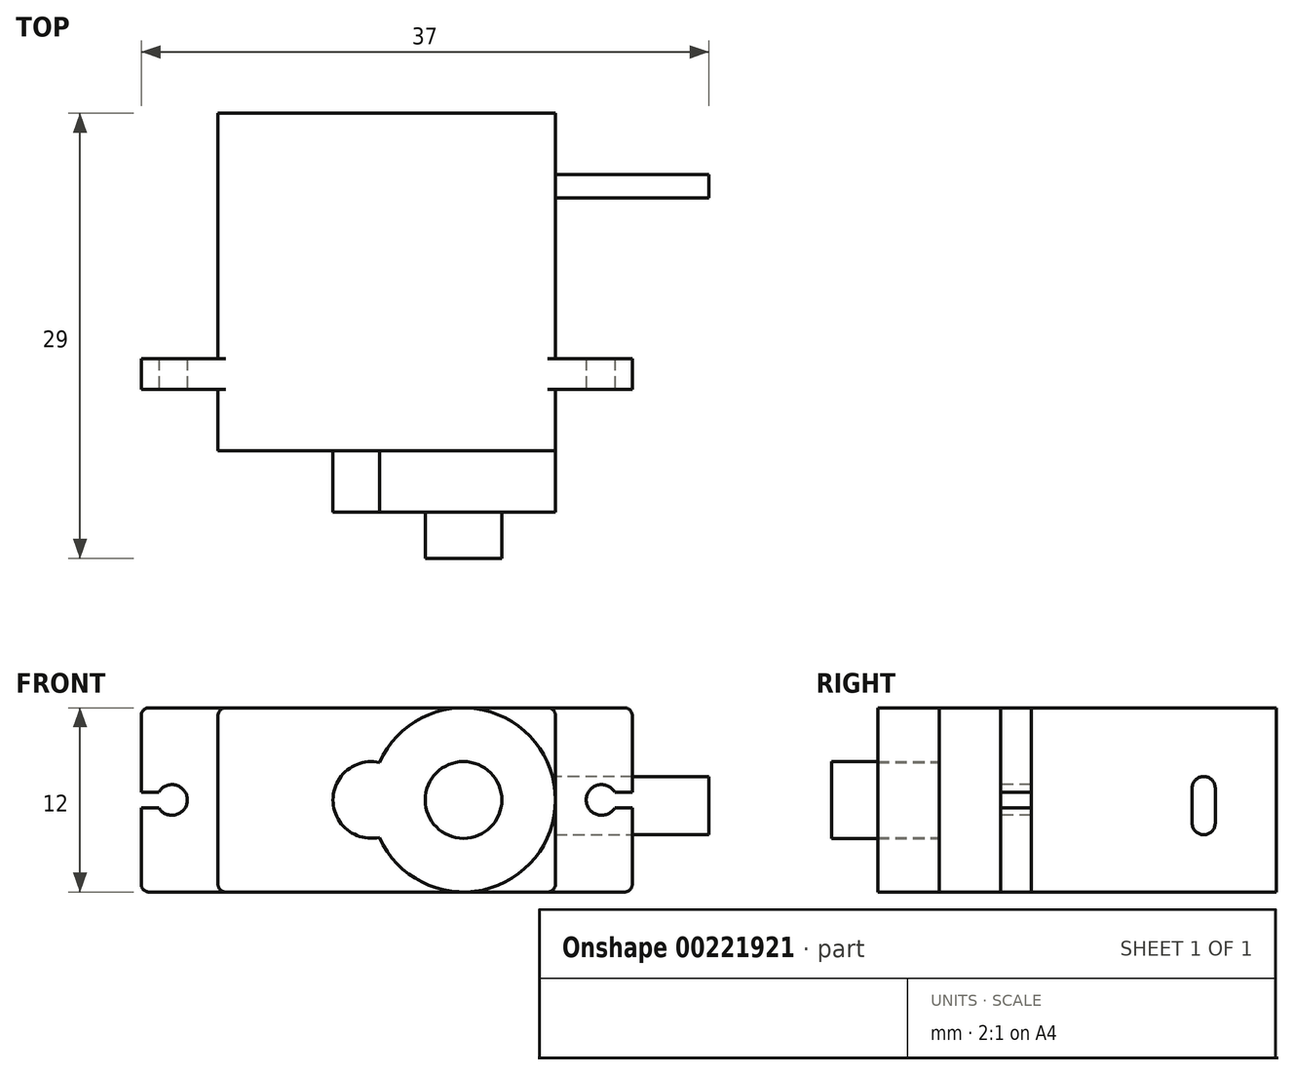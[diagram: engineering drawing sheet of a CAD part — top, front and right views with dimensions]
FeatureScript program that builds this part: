
annotation { "Feature Type Name" : "Feature", "Feature Type Description" : "" }
export const myFeature = defineFeature(function(context is Context, id is Id, definition is map)
    precondition{}
    {
        {
            var Q0;
            Q0=qCreatedBy(makeId("Top.planeOp"),FACE);
            var sketch = newSketch(context, id + "F0", { "sketchPlane" : qUnion([Q0])});
            skLineSegment(sketch, "E0.bottom", {"start": v(11, -11) * mm, "end": v(-11, -11) * mm});
            skLineSegment(sketch, "E0.top", {"start": v(11, 11) * mm, "end": v(-11, 11) * mm});
            skLineSegment(sketch, "E0.left", {"start": v(11, -11) * mm, "end": v(11, 11) * mm});
            skLineSegment(sketch, "E0.right", {"start": v(-11, -11) * mm, "end": v(-11, 11) * mm});
            skPoint(sketch, "E0.middle", {"position": v(0, 0) * mm});
            skLineSegment(sketch, "E1.bottom", {"start": v(-11, -7) * mm, "end": v(-16, -7) * mm});
            skLineSegment(sketch, "E1.top", {"start": v(-11, -5) * mm, "end": v(-16, -5) * mm});
            skLineSegment(sketch, "E1.left", {"start": v(-11, -7) * mm, "end": v(-11, -5) * mm});
            skLineSegment(sketch, "E1.right", {"start": v(-16, -7) * mm, "end": v(-16, -5) * mm});
            skLineSegment(sketch, "E2.bottom", {"start": v(11, -5) * mm, "end": v(16, -5) * mm});
            skLineSegment(sketch, "E2.top", {"start": v(11, -7) * mm, "end": v(16, -7) * mm});
            skLineSegment(sketch, "E2.left", {"start": v(11, -5) * mm, "end": v(11, -7) * mm});
            skLineSegment(sketch, "E2.right", {"start": v(16, -5) * mm, "end": v(16, -7) * mm});
            skSolve(sketch);
        }
        {
            var Q0;
            Q0 = qSketchRegion(id + "F0", true);
            extrude(context, id + "F1", {"entities" : qUnion([Q0]), "depth" : 12 * mm});
        }
        {
            var Q0;
            {var subQ0=sQuery(id+"F0.wireOp",EDGE,"E0.left");Q0=makeQuery(id+"F1.opExtrude","CAP_EDGE",EDGE,{"disambiguationData":[OSD([subQ0]),TDD([makeQuery(id+"F0.imprint","IMPRINT",EDGE,{"disambiguationData":[TD([[makeQuery(id+"F0.imprint","INTERSECT",VERTEX,{"derivedFrom":[sQuery(id+"F0.wireOp",EDGE,"E0.top"),subQ0]}),1.0]])],"derivedFrom":subQ0})])],"isStart":false});}
            var Q1;
            {var subQ0=sQuery(id+"F0.wireOp",EDGE,"E0.left");Q1=makeQuery(id+"F1.opExtrude","CAP_EDGE",EDGE,{"disambiguationData":[OSD([subQ0]),TDD([makeQuery(id+"F0.imprint","IMPRINT",EDGE,{"disambiguationData":[TD([[makeQuery(id+"F0.imprint","INTERSECT",VERTEX,{"derivedFrom":[sQuery(id+"F0.wireOp",EDGE,"E0.bottom"),subQ0]}),-1.0]])],"derivedFrom":subQ0})])],"isStart":false});}
            var Q2;
            {var subQ0=sQuery(id+"F0.wireOp",EDGE,"E0.right");Q2=makeQuery(id+"F1.opExtrude","CAP_EDGE",EDGE,{"disambiguationData":[OSD([subQ0]),TDD([makeQuery(id+"F0.imprint","IMPRINT",EDGE,{"disambiguationData":[TD([[makeQuery(id+"F0.imprint","INTERSECT",VERTEX,{"derivedFrom":[sQuery(id+"F0.wireOp",EDGE,"E0.bottom"),subQ0]}),-1.0]])],"derivedFrom":subQ0})])],"isStart":false});}
            var Q3;
            Q3=makeQuery(id+"F1.opExtrude","CAP_EDGE",EDGE,{"disambiguationData":[OSD([sQuery(id+"F0.wireOp",EDGE,"E2.right")])],"isStart":false});
            var Q4;
            {var subQ0=sQuery(id+"F0.wireOp",EDGE,"E0.right");Q4=makeQuery(id+"F1.opExtrude","CAP_EDGE",EDGE,{"disambiguationData":[OSD([subQ0]),TDD([makeQuery(id+"F0.imprint","IMPRINT",EDGE,{"disambiguationData":[TD([[makeQuery(id+"F0.imprint","INTERSECT",VERTEX,{"derivedFrom":[sQuery(id+"F0.wireOp",EDGE,"E0.top"),subQ0]}),1.0]])],"derivedFrom":subQ0})])],"isStart":false});}
            var Q5;
            Q5=makeQuery(id+"F1.opExtrude","CAP_EDGE",EDGE,{"disambiguationData":[OSD([sQuery(id+"F0.wireOp",EDGE,"E1.right")])],"isStart":false});
            var Q6;
            {var subQ0=sQuery(id+"F0.wireOp",EDGE,"E0.right");Q6=makeQuery(id+"F1.opExtrude","CAP_EDGE",EDGE,{"disambiguationData":[OSD([subQ0]),TDD([makeQuery(id+"F0.imprint","IMPRINT",EDGE,{"disambiguationData":[TD([[makeQuery(id+"F0.imprint","INTERSECT",VERTEX,{"derivedFrom":[sQuery(id+"F0.wireOp",EDGE,"E0.top"),subQ0]}),1.0]])],"derivedFrom":subQ0})])],"isStart":true});}
            var Q7;
            {var subQ0=sQuery(id+"F0.wireOp",EDGE,"E0.right");Q7=makeQuery(id+"F1.opExtrude","CAP_EDGE",EDGE,{"disambiguationData":[OSD([subQ0]),TDD([makeQuery(id+"F0.imprint","IMPRINT",EDGE,{"disambiguationData":[TD([[makeQuery(id+"F0.imprint","INTERSECT",VERTEX,{"derivedFrom":[sQuery(id+"F0.wireOp",EDGE,"E0.bottom"),subQ0]}),-1.0]])],"derivedFrom":subQ0})])],"isStart":true});}
            var Q8;
            Q8=makeQuery(id+"F1.opExtrude","CAP_EDGE",EDGE,{"disambiguationData":[OSD([sQuery(id+"F0.wireOp",EDGE,"E1.right")])],"isStart":true});
            var Q9;
            {var subQ0=sQuery(id+"F0.wireOp",EDGE,"E0.left");Q9=makeQuery(id+"F1.opExtrude","CAP_EDGE",EDGE,{"disambiguationData":[OSD([subQ0]),TDD([makeQuery(id+"F0.imprint","IMPRINT",EDGE,{"disambiguationData":[TD([[makeQuery(id+"F0.imprint","INTERSECT",VERTEX,{"derivedFrom":[sQuery(id+"F0.wireOp",EDGE,"E0.bottom"),subQ0]}),-1.0]])],"derivedFrom":subQ0})])],"isStart":true});}
            var Q10;
            {var subQ0=sQuery(id+"F0.wireOp",EDGE,"E0.left");Q10=makeQuery(id+"F1.opExtrude","CAP_EDGE",EDGE,{"disambiguationData":[OSD([subQ0]),TDD([makeQuery(id+"F0.imprint","IMPRINT",EDGE,{"disambiguationData":[TD([[makeQuery(id+"F0.imprint","INTERSECT",VERTEX,{"derivedFrom":[sQuery(id+"F0.wireOp",EDGE,"E0.top"),subQ0]}),1.0]])],"derivedFrom":subQ0})])],"isStart":true});}
            var Q11;
            Q11=makeQuery(id+"F1.opExtrude","CAP_EDGE",EDGE,{"disambiguationData":[OSD([sQuery(id+"F0.wireOp",EDGE,"E2.right")])],"isStart":true});
            fillet(context, id + "F2", {"entities" : qUnion([Q0, Q1, Q2, Q3, Q4, Q5, Q6, Q7, Q8, Q9, Q10, Q11]), "radius" : 0.5 * mm, "tangentPropagation" : true, "allowEdgeOverflow" : false});
        }
        {
            var Q0;
            Q0=makeQuery(id+"F1.opExtrude","SWEPT_FACE",FACE,{"disambiguationData":[OSD([sQuery(id+"F0.wireOp",EDGE,"E0.bottom")])]});
            var sketch = newSketch(context, id + "F3", { "sketchPlane" : qUnion([Q0])});
            skCircle(sketch, "E3", {"center": v(5, 6) * mm, "radius": 6 * mm});
            skCircle(sketch, "E4", {"center": v(-1, 6) * mm, "radius": 2.5 * mm});
            skSolve(sketch);
        }
        {
            var Q0;
            Q0 = qSketchRegion(id + "F3", true);
            extrude(context, id + "F4", {"entities" : qUnion([Q0]), "operationType" : NewBodyOperationType.ADD, "depth" : 4 * mm});
        }
        {
            var Q0;
            Q0=makeQuery(id+"F4.opExtrude","CAP_FACE",FACE,{"disambiguationData":[OSD([sQuery(id+"F3.wireOp",EDGE,"E3"),sQuery(id+"F3.wireOp",EDGE,"E4")])],"isStart":false});
            var sketch = newSketch(context, id + "F5", { "sketchPlane" : qUnion([Q0])});
            skCircle(sketch, "E5", {"center": v(5, 6) * mm, "radius": 2.5 * mm});
            skSolve(sketch);
        }
        {
            var Q0;
            Q0=makeQuery(id+"F5.imprint","IMPRINT",FACE,{"disambiguationData":[TD([[makeQuery(id+"F5.imprint","IMPRINT",EDGE,{"derivedFrom":sQuery(id+"F5.wireOp",EDGE,"E5")}),1.0]])]});
            extrude(context, id + "F6", {"entities" : qUnion([Q0]), "depth" : 3 * mm});
        }
        {
            var Q0;
            {var subQ0=sQuery(id+"F0.wireOp",EDGE,"E0.left");Q0=makeQuery(id+"F1.opExtrude","SWEPT_FACE",FACE,{"disambiguationData":[OSD([subQ0]),TDD([makeQuery(id+"F0.imprint","IMPRINT",EDGE,{"disambiguationData":[TD([[makeQuery(id+"F0.imprint","INTERSECT",VERTEX,{"derivedFrom":[sQuery(id+"F0.wireOp",EDGE,"E0.top"),subQ0]}),1.0]])],"derivedFrom":subQ0})])]});}
            var sketch = newSketch(context, id + "F7", { "sketchPlane" : qUnion([Q0])});
            skLineSegment(sketch, "E6.bottom", {"start": v(5.5, 3.73) * mm, "end": v(7, 3.73) * mm});
            skLineSegment(sketch, "E6.top", {"start": v(5.5, 7.53) * mm, "end": v(7, 7.53) * mm});
            skLineSegment(sketch, "E6.left", {"start": v(5.5, 3.73) * mm, "end": v(5.5, 7.53) * mm});
            skLineSegment(sketch, "E6.right", {"start": v(7, 3.73) * mm, "end": v(7, 7.53) * mm});
            skSolve(sketch);
        }
        {
            var Q0;
            Q0=makeQuery(id+"F7.imprint","IMPRINT",FACE,{"disambiguationData":[TD([[makeQuery(id+"F7.imprint","IMPRINT",EDGE,{"derivedFrom":sQuery(id+"F7.wireOp",EDGE,"E6.bottom")}),1.0]])]});
            extrude(context, id + "F8", {"entities" : qUnion([Q0]), "depth" : 10 * mm});
        }
        {
            var Q0;
            Q0=makeQuery(id+"F8.opExtrude","SWEPT_EDGE",EDGE,{"disambiguationData":[OSD([sQuery(id+"F7.wireOp",EDGE,"E6.top"),sQuery(id+"F7.wireOp",EDGE,"E6.left")])]});
            var Q1;
            Q1=makeQuery(id+"F8.opExtrude","SWEPT_EDGE",EDGE,{"disambiguationData":[OSD([sQuery(id+"F7.wireOp",EDGE,"E6.top"),sQuery(id+"F7.wireOp",EDGE,"E6.right")])]});
            var Q2;
            Q2=makeQuery(id+"F8.opExtrude","SWEPT_EDGE",EDGE,{"disambiguationData":[OSD([sQuery(id+"F7.wireOp",EDGE,"E6.bottom"),sQuery(id+"F7.wireOp",EDGE,"E6.left")])]});
            var Q3;
            Q3=makeQuery(id+"F8.opExtrude","SWEPT_EDGE",EDGE,{"disambiguationData":[OSD([sQuery(id+"F7.wireOp",EDGE,"E6.bottom"),sQuery(id+"F7.wireOp",EDGE,"E6.right")])]});
            fillet(context, id + "F9", {"entities" : qUnion([Q0, Q1, Q2, Q3]), "radius" : 0.75 * mm, "tangentPropagation" : true, "allowEdgeOverflow" : false});
        }
        {
            var Q0;
            Q0=makeQuery(id+"F1.opExtrude","SWEPT_FACE",FACE,{"disambiguationData":[OSD([sQuery(id+"F0.wireOp",EDGE,"E2.top")])]});
            var sketch = newSketch(context, id + "F10", { "sketchPlane" : qUnion([Q0])});
            skCircle(sketch, "E7", {"center": v(14, 6) * mm, "radius": 1 * mm});
            skPoint(sketch, "E7.centerSnap0", {"position": v(16, 6) * mm});
            skLineSegment(sketch, "E8.bottom", {"start": v(16, 6.5) * mm, "end": v(14, 6.5) * mm});
            skLineSegment(sketch, "E8.top", {"start": v(16, 5.5) * mm, "end": v(14, 5.5) * mm});
            skLineSegment(sketch, "E8.left", {"start": v(16, 6.5) * mm, "end": v(16, 5.5) * mm});
            skLineSegment(sketch, "E8.right", {"start": v(14, 6.5) * mm, "end": v(14, 5.5) * mm});
            skLineSegment(sketch, "E9", {"start": v(0, 12.23) * mm, "end": v(0, 0) * mm, "construction": true});
            skLineSegment(sketch, "E10.MirrorCS", {"start": v(-14, 6.5) * mm, "end": v(-14, 5.5) * mm});
            skLineSegment(sketch, "E11.MirrorCS", {"start": v(-16, 6.5) * mm, "end": v(-16, 5.5) * mm});
            skLineSegment(sketch, "E12.MirrorCS", {"start": v(-16, 6.5) * mm, "end": v(-14, 6.5) * mm});
            skLineSegment(sketch, "E13.MirrorCS", {"start": v(-16, 5.5) * mm, "end": v(-14, 5.5) * mm});
            skCircle(sketch, "E14.MirrorC", {"center": v(-14, 6) * mm, "radius": 1 * mm});
            skPoint(sketch, "E15.MirrorP", {"position": v(-16, 6) * mm});
            skSolve(sketch);
        }
        {
            var Q0;
            {var subQ5=sQuery(id+"F10.wireOp",EDGE,"E8.right");Q0=makeQuery(id+"F10.imprint","IMPRINT",FACE,{"disambiguationData":[TD([[makeQuery(id+"F10.imprint","IMPRINT",EDGE,{"derivedFrom":subQ5}),1.0]])]});}
            var Q1;
            {var subQ5=sQuery(id+"F10.wireOp",EDGE,"E8.right");Q1=makeQuery(id+"F10.imprint","IMPRINT",FACE,{"disambiguationData":[TD([[makeQuery(id+"F10.imprint","IMPRINT",EDGE,{"derivedFrom":subQ5}),-1.0]])]});}
            var Q2;
            {var subQ5=sQuery(id+"F10.wireOp",EDGE,"E8.left");Q2=makeQuery(id+"F10.imprint","IMPRINT",FACE,{"disambiguationData":[TD([[makeQuery(id+"F10.imprint","IMPRINT",EDGE,{"derivedFrom":subQ5}),-1.0]])]});}
            var Q3;
            {var subQ0=sQuery(id+"F10.wireOp",EDGE,"E10.MirrorCS");Q3=makeQuery(id+"F10.imprint","IMPRINT",FACE,{"disambiguationData":[TD([[makeQuery(id+"F10.imprint","IMPRINT",EDGE,{"derivedFrom":subQ0}),1.0]])]});}
            var Q4;
            {var subQ0=sQuery(id+"F10.wireOp",EDGE,"E11.MirrorCS");Q4=makeQuery(id+"F10.imprint","IMPRINT",FACE,{"disambiguationData":[TD([[makeQuery(id+"F10.imprint","IMPRINT",EDGE,{"derivedFrom":subQ0}),1.0]])]});}
            var Q5;
            {var subQ0=sQuery(id+"F10.wireOp",EDGE,"E10.MirrorCS");Q5=makeQuery(id+"F10.imprint","IMPRINT",FACE,{"disambiguationData":[TD([[makeQuery(id+"F10.imprint","IMPRINT",EDGE,{"derivedFrom":subQ0}),-1.0]])]});}
            var Q6;
            Q6=makeQuery(id+"F1.opExtrude","SWEPT_FACE",FACE,{"disambiguationData":[OSD([sQuery(id+"F0.wireOp",EDGE,"E2.bottom")])]});
            extrude(context, id + "F11", {"entities" : qUnion([Q0, Q1, Q2, Q3, Q4, Q5]), "operationType" : NewBodyOperationType.REMOVE, "endBound" : BoundingType.UP_TO_SURFACE, "oppositeDirection" : true, "endBoundEntityFace" : qUnion([Q6]), "depth" : 25 * mm});
        }
    });
